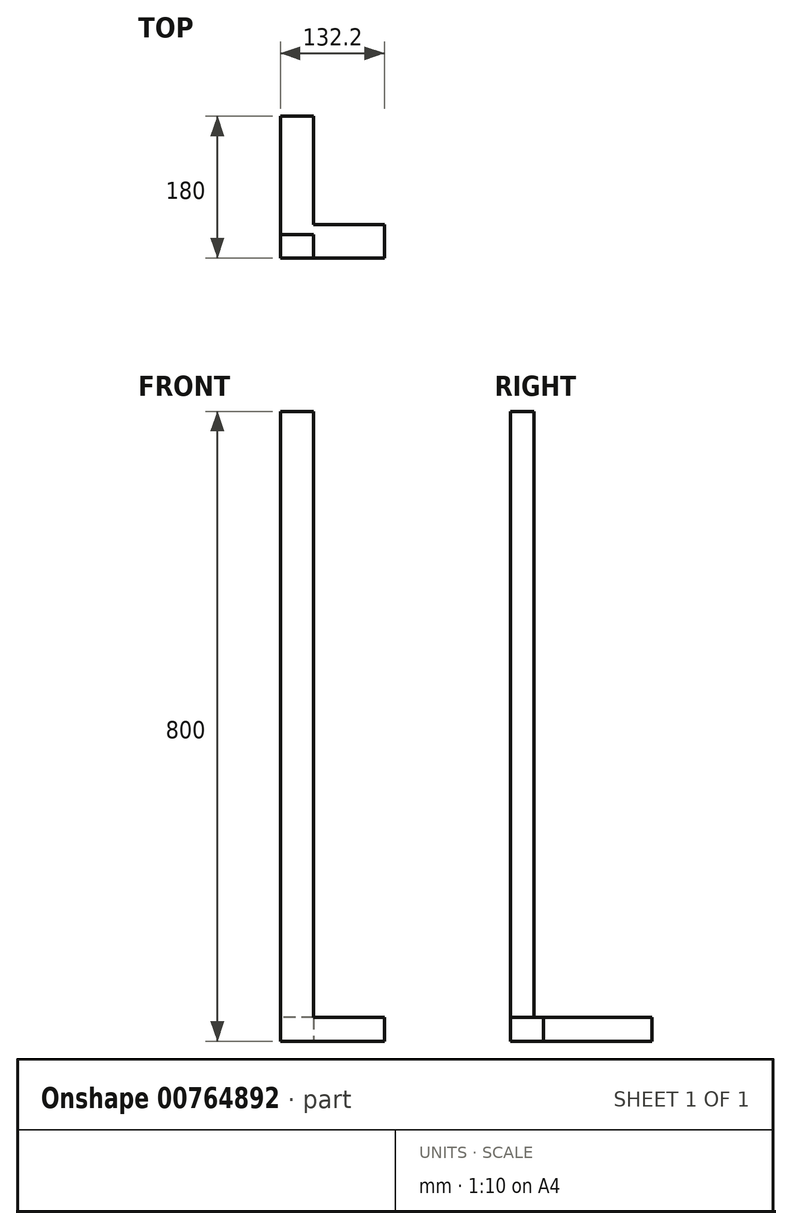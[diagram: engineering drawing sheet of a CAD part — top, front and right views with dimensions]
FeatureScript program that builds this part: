
annotation { "Feature Type Name" : "Feature", "Feature Type Description" : "" }
export const myFeature = defineFeature(function(context is Context, id is Id, definition is map)
    precondition{}
    {
        {
            var Q0;
            Q0=qCreatedBy(makeId("Top.planeOp"),FACE);
            var sketch = newSketch(context, id + "F0", { "sketchPlane" : qUnion([Q0])});
            skLineSegment(sketch, "E0.bottom", {"start": v(21.1, -15) * mm, "end": v(-21.1, -15) * mm});
            skLineSegment(sketch, "E0.top", {"start": v(21.1, 15) * mm, "end": v(-21.1, 15) * mm});
            skLineSegment(sketch, "E0.left", {"start": v(21.1, -15) * mm, "end": v(21.1, 15) * mm});
            skLineSegment(sketch, "E0.right", {"start": v(-21.1, -15) * mm, "end": v(-21.1, 15) * mm});
            skPoint(sketch, "E0.middle", {"position": v(0, 0) * mm});
            skLineSegment(sketch, "E1", {"start": v(-21.1, 15) * mm, "end": v(-21.1, 165) * mm});
            skLineSegment(sketch, "E2", {"start": v(-21.1, 165) * mm, "end": v(21.1, 165) * mm});
            skLineSegment(sketch, "E3", {"start": v(21.1, 165) * mm, "end": v(21.1, 15) * mm});
            skLineSegment(sketch, "E4", {"start": v(21.1, -15) * mm, "end": v(111.1, -15) * mm});
            skLineSegment(sketch, "E5", {"start": v(111.1, -15) * mm, "end": v(111.1, 27.2) * mm});
            skLineSegment(sketch, "E6", {"start": v(111.1, 27.2) * mm, "end": v(21.1, 27.2) * mm});
            skSolve(sketch);
        }
        {
            var Q0;
            Q0=makeQuery(id+"F0.imprint","IMPRINT",FACE,{"disambiguationData":[TD([[makeQuery(id+"F0.imprint","IMPRINT",EDGE,{"derivedFrom":sQuery(id+"F0.wireOp",EDGE,"E0.bottom")}),-1.0]])]});
            extrude(context, id + "F1", {"entities" : qUnion([Q0]), "depth" : 800 * mm, "offsetDistance" : 25 * mm});
        }
        {
            var Q0;
            {var subQ1=sQuery(id+"F0.wireOp",EDGE,"E0.left");Q0=makeQuery(id+"F0.imprint","IMPRINT",FACE,{"disambiguationData":[TD([[makeQuery(id+"F0.imprint","IMPRINT",EDGE,{"derivedFrom":subQ1}),-1.0]])]});}
            var Q1;
            {var subQ3=sQuery(id+"F0.wireOp",EDGE,"E0.top");Q1=makeQuery(id+"F0.imprint","IMPRINT",FACE,{"disambiguationData":[TD([[makeQuery(id+"F0.imprint","IMPRINT",EDGE,{"derivedFrom":subQ3}),-1.0]])]});}
            extrude(context, id + "F2", {"entities" : qUnion([Q0, Q1]), "operationType" : NewBodyOperationType.ADD, "depth" : 30 * mm, "offsetDistance" : 25 * mm});
        }
    });
